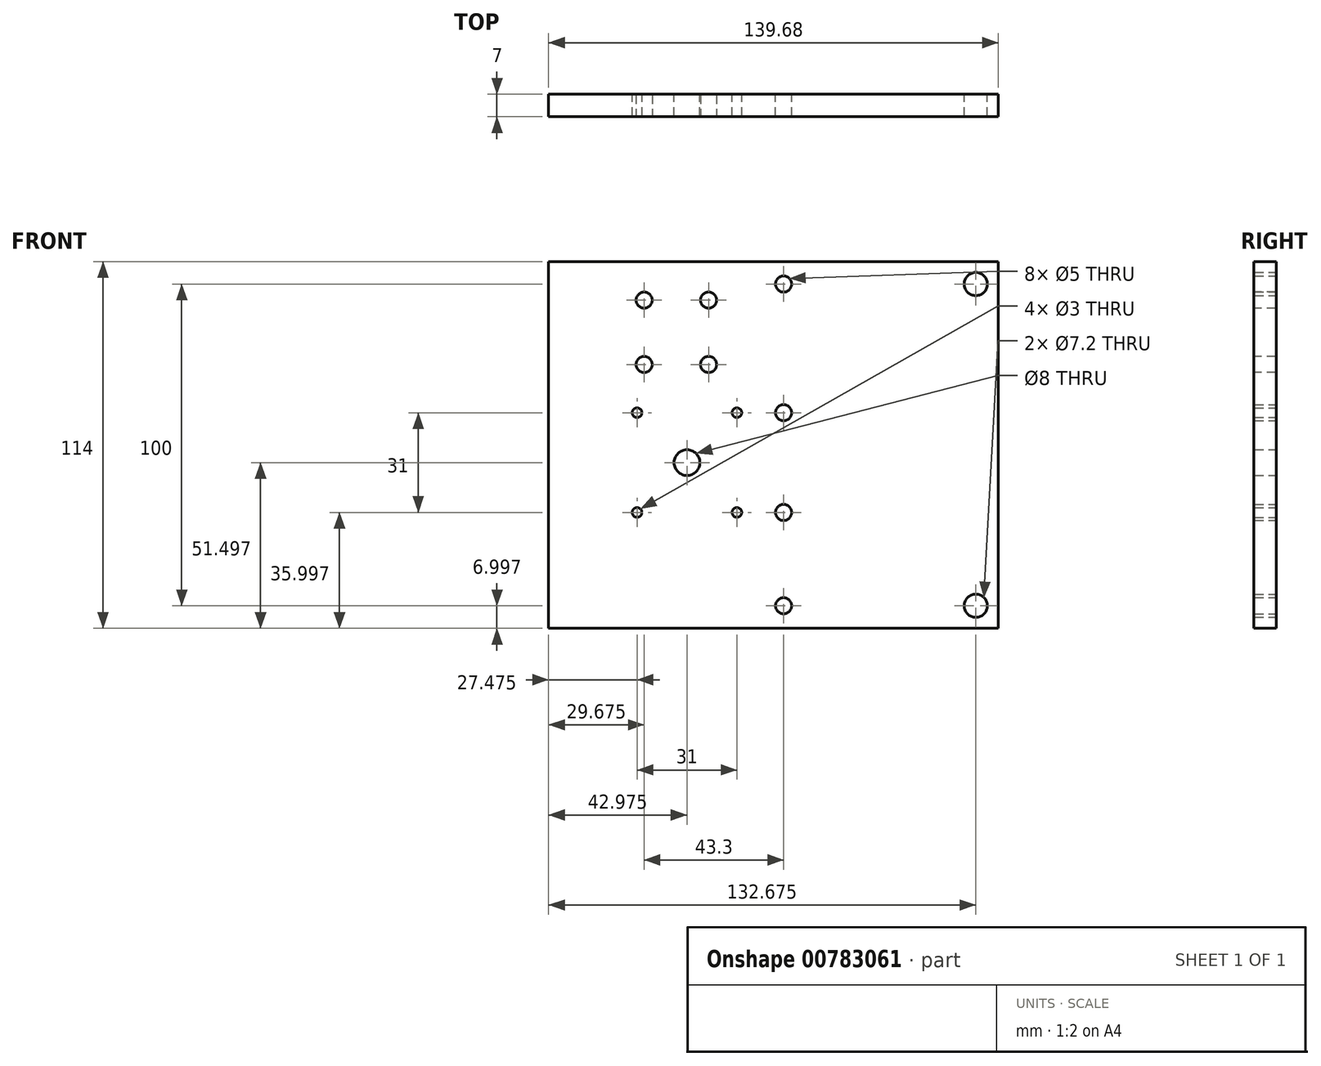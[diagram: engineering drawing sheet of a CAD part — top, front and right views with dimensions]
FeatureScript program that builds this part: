
annotation { "Feature Type Name" : "Feature", "Feature Type Description" : "" }
export const myFeature = defineFeature(function(context is Context, id is Id, definition is map)
    precondition{}
    {
        {
            var Q0;
            Q0=qCreatedBy(makeId("Front.planeOp"),FACE);
            var sketch = newSketch(context, id + "F0", { "sketchPlane" : qUnion([Q0])});
            skLineSegment(sketch, "E0.bottom", {"start": v(-151.94, 93.54) * mm, "end": v(4.76, 93.54) * mm});
            skLineSegment(sketch, "E0.top", {"start": v(-151.94, -20.46) * mm, "end": v(4.76, -20.46) * mm});
            skLineSegment(sketch, "E0.left", {"start": v(-151.94, 93.54) * mm, "end": v(-151.94, -20.46) * mm});
            skLineSegment(sketch, "E0.right", {"start": v(4.76, 93.54) * mm, "end": v(4.76, -20.46) * mm});
            skCircle(sketch, "E1", {"center": v(-61.94, -13.46) * mm, "radius": 2.5 * mm});
            skCircle(sketch, "E2", {"center": v(-2.24, -13.46) * mm, "radius": 3.6 * mm});
            skCircle(sketch, "E3.0.1.0", {"center": v(-61.94, 86.54) * mm, "radius": 2.5 * mm});
            skCircle(sketch, "E3.0.1.1", {"center": v(-2.24, 86.54) * mm, "radius": 3.6 * mm});
            skLineSegment(sketch, "E3.direction1", {"start": v(-61.94, -13.46) * mm, "end": v(-36.94, -13.46) * mm, "construction": true});
            skLineSegment(sketch, "E3.direction2", {"start": v(-61.94, -13.46) * mm, "end": v(-61.94, 86.54) * mm, "construction": true});
            skCircle(sketch, "E4", {"center": v(-91.94, 31.04) * mm, "radius": 11 * mm});
            skCircle(sketch, "E5", {"center": v(-76.44, 46.54) * mm, "radius": 1.5 * mm});
            skCircle(sketch, "E6", {"center": v(-76.44, 15.54) * mm, "radius": 1.5 * mm});
            skCircle(sketch, "E7", {"center": v(-107.44, 15.54) * mm, "radius": 1.5 * mm});
            skCircle(sketch, "E8", {"center": v(-107.44, 46.54) * mm, "radius": 1.5 * mm});
            skCircle(sketch, "E9", {"center": v(-61.94, 46.54) * mm, "radius": 2.5 * mm});
            skCircle(sketch, "E10", {"center": v(-61.94, 15.54) * mm, "radius": 2.5 * mm});
            skCircle(sketch, "E11", {"center": v(-91.94, 31.04) * mm, "radius": 4 * mm});
            skSolve(sketch);
        }
        {
            var Q0;
            Q0=makeQuery(id+"F0.imprint","IMPRINT",FACE,{"disambiguationData":[TD([[makeQuery(id+"F0.imprint","IMPRINT",EDGE,{"derivedFrom":sQuery(id+"F0.wireOp",EDGE,"E0.bottom")}),-1.0]])]});
            var Q1;
            Q1=makeQuery(id+"F0.imprint","IMPRINT",FACE,{"disambiguationData":[TD([[makeQuery(id+"F0.imprint","IMPRINT",EDGE,{"derivedFrom":sQuery(id+"F0.wireOp",EDGE,"E4")}),1.0]])]});
            extrude(context, id + "F1", {"entities" : qUnion([Q0, Q1]), "depth" : 7 * mm, "offsetDistance" : 25 * mm});
        }
        {
            var Q0;
            Q0=makeQuery(id+"F1.opExtrude","CAP_FACE",FACE,{"disambiguationData":[OSD([sQuery(id+"F0.wireOp",EDGE,"E0.bottom"),sQuery(id+"F0.wireOp",EDGE,"E0.top"),sQuery(id+"F0.wireOp",EDGE,"E0.left"),sQuery(id+"F0.wireOp",EDGE,"E0.right"),sQuery(id+"F0.wireOp",EDGE,"E1"),sQuery(id+"F0.wireOp",EDGE,"E2"),sQuery(id+"F0.wireOp",EDGE,"E3.0.1.0"),sQuery(id+"F0.wireOp",EDGE,"E3.0.1.1"),sQuery(id+"F0.wireOp",EDGE,"E5"),sQuery(id+"F0.wireOp",EDGE,"E6"),sQuery(id+"F0.wireOp",EDGE,"E7"),sQuery(id+"F0.wireOp",EDGE,"E8"),sQuery(id+"F0.wireOp",EDGE,"E9"),sQuery(id+"F0.wireOp",EDGE,"E10"),sQuery(id+"F0.wireOp",EDGE,"E11")])],"isStart":false});
            var sketch = newSketch(context, id + "F2", { "sketchPlane" : qUnion([Q0])});
            skCircle(sketch, "E12", {"center": v(-105.24, 81.54) * mm, "radius": 2.5 * mm});
            skCircle(sketch, "E13", {"center": v(-85.24, 81.54) * mm, "radius": 2.5 * mm});
            skCircle(sketch, "E14", {"center": v(-105.24, 61.54) * mm, "radius": 2.5 * mm});
            skCircle(sketch, "E15", {"center": v(-85.24, 61.54) * mm, "radius": 2.5 * mm});
            skLineSegment(sketch, "E16.bottom", {"start": v(-112.24, 102.29) * mm, "end": v(-134.92, 102.29) * mm});
            skLineSegment(sketch, "E16.top", {"start": v(-112.24, -39.08) * mm, "end": v(-134.92, -39.08) * mm});
            skLineSegment(sketch, "E16.left", {"start": v(-112.24, 102.29) * mm, "end": v(-112.24, -39.08) * mm});
            skLineSegment(sketch, "E16.right", {"start": v(-134.92, 102.29) * mm, "end": v(-134.92, -39.08) * mm});
            skSolve(sketch);
        }
        {
            var Q0;
            Q0=makeQuery(id+"F2.imprint","IMPRINT",FACE,{"disambiguationData":[TD([[makeQuery(id+"F2.imprint","IMPRINT",EDGE,{"derivedFrom":sQuery(id+"F2.wireOp",EDGE,"E12")}),1.0]])]});
            var Q1;
            Q1=makeQuery(id+"F2.imprint","IMPRINT",FACE,{"disambiguationData":[TD([[makeQuery(id+"F2.imprint","IMPRINT",EDGE,{"derivedFrom":sQuery(id+"F2.wireOp",EDGE,"E14")}),1.0]])]});
            var Q2;
            Q2=makeQuery(id+"F2.imprint","IMPRINT",FACE,{"disambiguationData":[TD([[makeQuery(id+"F2.imprint","IMPRINT",EDGE,{"derivedFrom":sQuery(id+"F2.wireOp",EDGE,"E15")}),1.0]])]});
            var Q3;
            Q3=makeQuery(id+"F2.imprint","IMPRINT",FACE,{"disambiguationData":[TD([[makeQuery(id+"F2.imprint","IMPRINT",EDGE,{"derivedFrom":sQuery(id+"F2.wireOp",EDGE,"E13")}),1.0]])]});
            var Q4;
            {var subQ5=makeQuery(id+"F1.opExtrude","CAP_EDGE",EDGE,{"disambiguationData":[OSD([sQuery(id+"F0.wireOp",EDGE,"E0.left")])],"isStart":false});Q4=makeQuery(id+"F2.imprint","IMPRINT",FACE,{"disambiguationData":[TD([[makeQuery(id+"F2.imprint","IMPRINT",EDGE,{"derivedFrom":subQ5}),1.0]])]});}
            extrude(context, id + "F3", {"entities" : qUnion([Q0, Q1, Q2, Q3, Q4]), "operationType" : NewBodyOperationType.REMOVE, "oppositeDirection" : true, "depth" : 25 * mm, "offsetDistance" : 25 * mm});
        }
    });
